# Revit family: Hekatron_Rauchwarnmelder_FH.Genius _DE_22.01
name_source: partatom
category: Brandmelder
revit_build: Autodesk Revit 2018 (Build: 20190510_1515(x64)
units: mm (PartAtom-declared; Revit-internal decimal feet)

## family parameters
Basisbauteil = Fläche
Beim Laden mit Abzugskörper schneiden = Nein
Bemaßung runder Anschluss = Durchmesser verwenden
Beschriftungsausrichtung beibehalten = Ja
Gemeinsam genutzt = Nein
OmniClass-Nummer = 23.85.30.21
OmniClass-Titel = Environmental Detection/Registration
Raumberechnungspunkt = Nein
Teiletyp = Normal

## types (1)
- FH.Genius
    Beschreibung = Hausalarm und Funkinterface in einem Gerät. Ergänzung eines Genius Funknetzwerks zur flächendeckenden Alarmierung im Ereignisfall. Bestehende Genius-Funksysteme können erweitert werden.
    Betriebsspannung = 10 bis 30 V DC
    Breite (mm) = 130.0
    Farbe = blau, ähnlich RAL 5005
    Funktionsprinzip = Funk
    Hersteller = Hekatron
    Höhe (mm) = 130.0
    Kabeleinführung = oben, unten
    Lautstärke DIN-Ton (dB) = 50.0
    Link zu Ausschreibungstext = https://www.meinhplus.de
    Link zu ausschreiben.de = https://www.ausschreiben.de
    Link zum Datenblatt = https://www.hekatron-planungstools.de
    Material = PC-ABS
    Modell = FH.Genius
    Montageart = Aufputz
    Nettogewicht (g) = 201.0
    Schutzart = IP 41
    Tiefe (mm) = 32.0
    Typenkommentare = Funkhandtaster für Funksystem Genius
    UB A&S Artikel Nummer = 31-5000013-01-03
    URL = https://www.hekatron-brandschutz.de
    Version des BIM Objektes = 22.01
    Vorgabe-Ansicht = 1200 mm
    Zulässige Umgebungstemperatur = 0 °C bis + 55 °C

## geometry (parser evidence)
native form markers: Sweep x1
no freeform markers — native parametric forms only
